# Revit family: CONV_Wexiodisk_Dishwasher_WD-7-DuplusEcoFlow
name_source: partatom
category: Specialty Equipment
revit_build: Autodesk Revit 2016 (Build: 20150714_1515(x64)
units: mm (PartAtom-declared; Revit-internal decimal feet)

## family parameters
Always vertical = Yes
Cut with Voids When Loaded = No
OmniClass Number = 23.45.30.14.11
OmniClass Title = Commercial Dishwashers
Part Type = Normal
Room Calculation Point = No
Round Connector Dimension = Use Diameter
Shared = No
Work Plane-Based = No

## types (1)
- WD-7 Duplus ECO-FLOW
    AssetType = Fixed
    BIMObjectName = CONV_Wexiodisk_Dishwasher_WD-7-DuplusEcoFlow
    BasketSize = 500x500mm
    BoosterHeater = 9000 W
    Brand = Wexiodisk
    CapacityBasketsPerHour = 50
    Category = Hood type dishwashing machines
    Color = Grey
    ConvergoRefNr = 0100-1703-0005-SE
    Cost = 0 $
    DishwasherMainMaterial = Stainless Steel
    DishwasherSecondaryMaterial = Black Plastic
    DrainConnectionHose = 50.00 mm
    DurationUnit = Year
    ElectricalDeviceNominalPower = 0 W
    ExpiringDate = 12/2018
    Features = Alternative water connection from below,Water outlet for detergent, Plugged hole for detergent hose
    FloorDrain = 3.0 L/s
    HasProtectiveEarth = No
    HeatLoadToRoomLatent = 500 W
    HeatLoadToRoomSensible = 1200 W
    HeatLoadToRoomTotal = 1700 W
    IP_Code = 45
    IfcExportAs = NOTDEFINED
    IfcExportType = IfcFurnitureType
    MainFuse(400V-3N) = 16 A
    ManufacterURL = https://www.wexiodisk.com
    Manufacturer = Wexiödisk
    ManufacturerName = Wexiodisk
    Material = Stainless Steel
    Model = WD-7 Duplus ECO-FLOW
    NBSDescription = Commercial passthrough dishwashers
    NBSReference = 45-35-15/422
    Name = Dishwasher_WD-7-DuplusEcoFlow
    NominalCurrent = 0 A
    NominalDepth = 800 mm  [stored 2.62467 ft]
    NominalFrequencyRange = 0 Hz
    NominalHeight = 2146 mm  [stored 7.04068 ft]
    NominalVoltage = 400 V
    NominalWidth = 755 mm
    NumberOfPoles = 0
    PhaseAngle = 0.00°
    PumpFinalRinse = 670 W
    PumpRecirculatedRinse = 670 W
    Revision = 2
    Shape = Cube
    Size = 755x800x2146mm
    SoundLevel = 63 dB
    TankHeater = 5400 W
    TankVolume = 50.0 L
    TankVolumeChemicalWash = 45.0 L
    TankVolumeRecirculatedRinse = 5.5 L
    URL = https://www.wexiodisk.com
    Uniclass2 = Pr_40_70_21_60
    Uniclass2015Description = Pass-through dishwashers
    Uniclass2015Reference = Pr_40_70_21_60
    UsageCurrent = 0 A
    Version = 2
    VersionDate = 01/01/2018
    WarrantyDurationUnit = Year
    WashPump = 1100 W
    WaterCapacityFlow = 0.8 L/s
    WaterCapacityPressure = 20000.0 Pa
    WaterConnection(5-70°) = R1/2"
    WaterConsumptionRinse/Programme = 1.5 L
    WaterQuality = 2-7 °dH
    WeightMachineInOperation = 195kg

note: [stored X ft] marks values corroborated as IEEE doubles in the binary element streams (Revit-internal decimal feet)

## geometry (parser evidence)
native form markers: Blend x4, Sweep x1
no freeform markers — native parametric forms only
